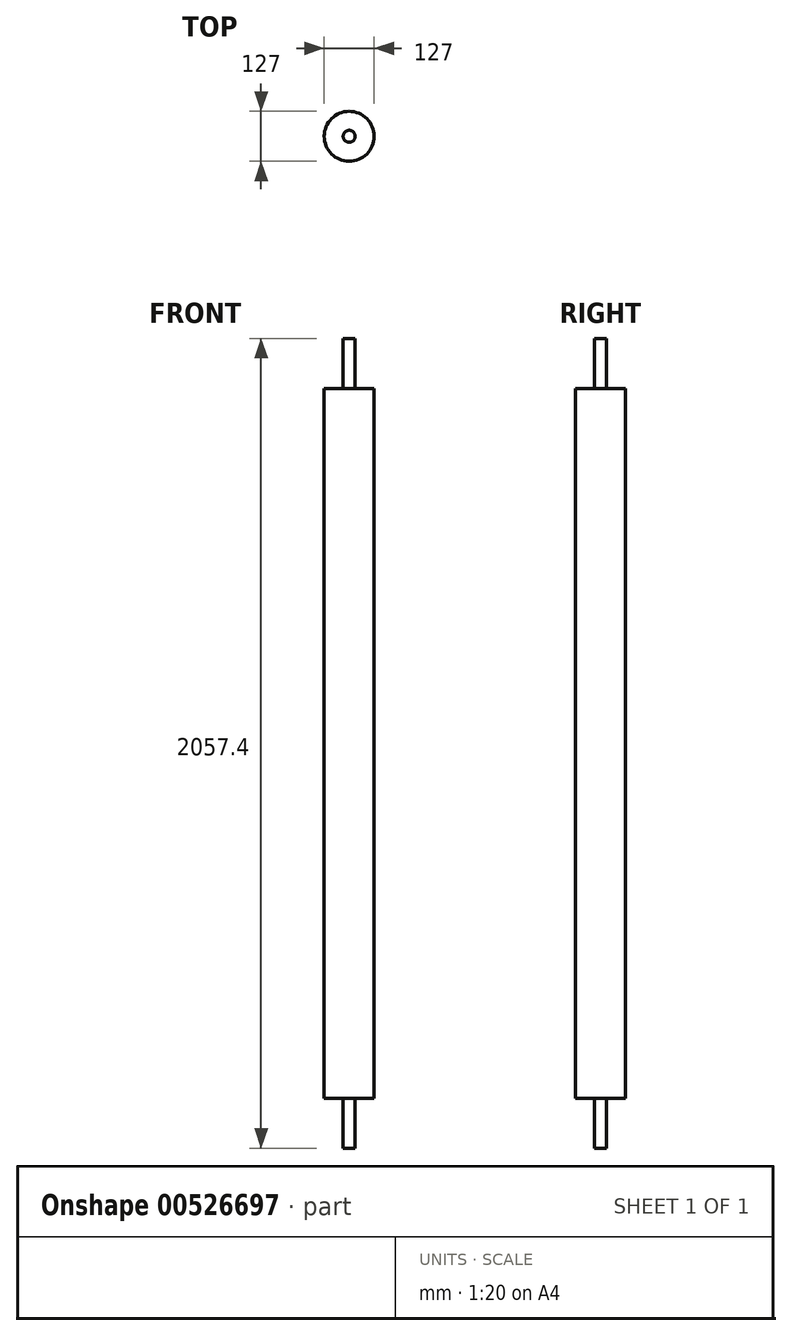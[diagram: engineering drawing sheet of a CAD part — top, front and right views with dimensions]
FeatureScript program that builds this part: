
annotation { "Feature Type Name" : "Feature", "Feature Type Description" : "" }
export const myFeature = defineFeature(function(context is Context, id is Id, definition is map)
    precondition{}
    {
        {
            var Q0;
            Q0=qCreatedBy(makeId("Top.planeOp"),FACE);
            var sketch = newSketch(context, id + "F0", { "sketchPlane" : qUnion([Q0])});
            skCircle(sketch, "E0", {"center": v(0, 0) * mm, "radius": 63.5 * mm});
            skSolve(sketch);
        }
        {
            var Q0;
            Q0=makeQuery(id+"F0.imprint","IMPRINT",FACE,{"disambiguationData":[TD([[makeQuery(id+"F0.imprint","IMPRINT",EDGE,{"derivedFrom":sQuery(id+"F0.wireOp",EDGE,"E0")}),1.0]])]});
            extrude(context, id + "F1", {"entities" : qUnion([Q0]), "depth" : 1803.4 * mm, "offsetDistance" : 25.4 * mm});
        }
        {
            var Q0;
            Q0=makeQuery(id+"F1.opExtrude","CAP_FACE",FACE,{"disambiguationData":[OSD([sQuery(id+"F0.wireOp",EDGE,"E0")])],"isStart":false});
            cPlane(context, id + "F2", {"entities" : qUnion([Q0]), "cplaneType" : CPlaneType.OFFSET, "offset" : 0 * mm, "width" : 152.4 * mm, "height" : 152.4 * mm});
        }
        {
            var Q0;
            Q0=qCreatedBy(id+"F2.planeOp",FACE);
            var sketch = newSketch(context, id + "F3", { "sketchPlane" : qUnion([Q0])});
            skCircle(sketch, "E1", {"center": v(0, 0) * mm, "radius": 15.24 * mm});
            skSolve(sketch);
        }
        {
            var Q0;
            Q0=makeQuery(id+"F3.imprint","IMPRINT",FACE,{"disambiguationData":[TD([[makeQuery(id+"F3.imprint","IMPRINT",EDGE,{"derivedFrom":sQuery(id+"F3.wireOp",EDGE,"E1")}),1.0]])]});
            extrude(context, id + "F4", {"entities" : qUnion([Q0]), "operationType" : NewBodyOperationType.ADD, "depth" : 127 * mm, "offsetDistance" : 25.4 * mm});
        }
        {
            var Q0;
            Q0=qCreatedBy(makeId("Top.planeOp"),FACE);
            var sketch = newSketch(context, id + "F5", { "sketchPlane" : qUnion([Q0])});
            skCircle(sketch, "E2", {"center": v(0, 0) * mm, "radius": 15.24 * mm});
            skSolve(sketch);
        }
        {
            var Q0;
            Q0 = qSketchRegion(id + "F5", true);
            extrude(context, id + "F6", {"entities" : qUnion([Q0]), "operationType" : NewBodyOperationType.ADD, "oppositeDirection" : true, "depth" : 127 * mm, "offsetDistance" : 25.4 * mm});
        }
    });
